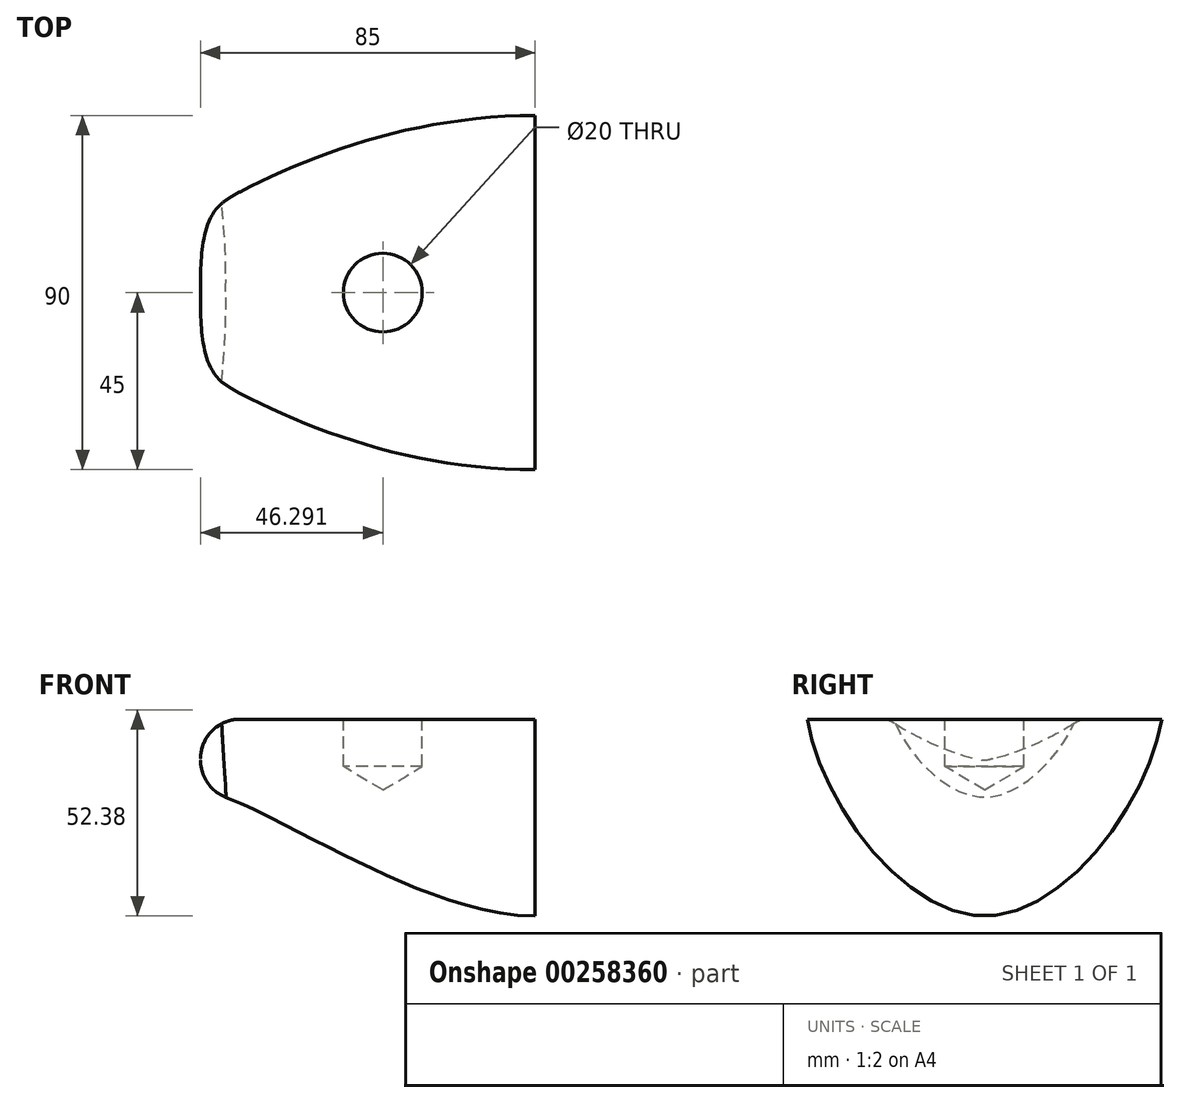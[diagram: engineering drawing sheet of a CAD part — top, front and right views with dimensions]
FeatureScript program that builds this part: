
annotation { "Feature Type Name" : "Feature", "Feature Type Description" : "" }
export const myFeature = defineFeature(function(context is Context, id is Id, definition is map)
    precondition{}
    {
        {
            var Q0;
            Q0=qCreatedBy(makeId("Right.planeOp"),FACE);
            cPlane(context, id + "F0", {"entities" : qUnion([Q0]), "cplaneType" : CPlaneType.OFFSET, "offset" : 85 * mm, "oppositeDirection" : true, "width" : 150 * mm, "height" : 150 * mm});
        }
        {
            var Q0;
            Q0=qCreatedBy(makeId("Right.planeOp"),FACE);
            var sketch = newSketch(context, id + "F1", { "sketchPlane" : qUnion([Q0])});
            skFitSpline(sketch, "E0", {"points": [v(-45, 0) * mm, v(0, -50) * mm, v(45, 0) * mm], "startDerivative": vector(18, -120) * mm, "endDerivative": vector(18, 120) * mm});
            skLineSegment(sketch, "E1", {"start": v(45, 0) * mm, "end": v(-45, 0) * mm});
            skPoint(sketch, "E2", {"position": v(0, 0) * mm});
            skSolve(sketch);
        }
        {
            var Q0;
            Q0=qCreatedBy(id+"F0.planeOp",FACE);
            var sketch = newSketch(context, id + "F2", { "sketchPlane" : qUnion([Q0])});
            skFitSpline(sketch, "E3", {"points": [v(-20, 0) * mm, v(0, -18) * mm, v(20, 0) * mm], "startDerivative": vector(12, -30) * mm, "endDerivative": vector(12, 30) * mm});
            skLineSegment(sketch, "E4", {"start": v(-20, 0) * mm, "end": v(20, 0) * mm});
            skLineSegment(sketch, "E5", {"start": v(20, 0) * mm, "end": v(-20, 0) * mm});
            skPoint(sketch, "E6", {"position": v(0, 0) * mm});
            skPoint(sketch, "E7.0", {"position": v(0, -50) * mm});
            skSolve(sketch);
        }
        {
            var Q0;
            Q0=qCreatedBy(makeId("Top.planeOp"),FACE);
            var sketch = newSketch(context, id + "F3", { "sketchPlane" : qUnion([Q0])});
            skPoint(sketch, "E8", {"position": v(0, -45) * mm});
            skPoint(sketch, "E9", {"position": v(0, 0) * mm});
            skPoint(sketch, "E10", {"position": v(0, 45) * mm});
            skPoint(sketch, "E11.orphan", {"position": v(-102.76, 0) * mm});
            skPoint(sketch, "E12.endDerivative.orphan", {"position": v(-78.5, -38.65) * mm});
            skPoint(sketch, "E13.MirrorCS.end.orphan", {"position": v(-85, 20) * mm});
            skPoint(sketch, "E14.end.orphan", {"position": v(-85, -20) * mm});
            skPoint(sketch, "E15.endDerivative.orphan", {"position": v(-65, 32) * mm});
            skPoint(sketch, "E15.startDerivative.orphan", {"position": v(-35, 45) * mm});
            skFitSpline(sketch, "E16", {"points": [v(-85, -20) * mm, v(0, -45) * mm], "startDerivative": vector(60, -36) * mm, "endDerivative": vector(105, 0) * mm});
            skFitSpline(sketch, "E17.MirrorCS", {"points": [v(-85, 20) * mm, v(0, 45) * mm], "startDerivative": vector(60, 36) * mm, "endDerivative": vector(105, 0) * mm});
            skPoint(sketch, "E18", {"position": v(-37.86, 0) * mm});
            skSolve(sketch);
        }
        {
            var Q0;
            Q0=qCreatedBy(makeId("Front.planeOp"),FACE);
            var sketch = newSketch(context, id + "F4", { "sketchPlane" : qUnion([Q0])});
            skPoint(sketch, "E19.0.internal.orphan", {"position": v(0, -26.5) * mm});
            skPoint(sketch, "E20", {"position": v(-55.09, -17.88) * mm});
            skPoint(sketch, "E21", {"position": v(-55.09, -15.07) * mm});
            skPoint(sketch, "E22.0.internal.orphan", {"position": v(0, -50) * mm});
            skPoint(sketch, "E22.endDerivative.orphan", {"position": v(-70, -20) * mm});
            skPoint(sketch, "E22.startDerivative.orphan", {"position": v(-14.43, -50) * mm});
            skPoint(sketch, "E23.0", {"position": v(-85, -18) * mm});
            skFitSpline(sketch, "E24", {"points": [v(-85, -18) * mm, v(0, -50) * mm], "startDerivative": vector(45, -6) * mm, "endDerivative": vector(89.92, 0) * mm});
            skSolve(sketch);
        }
        {
            var Q0;
            Q0=makeQuery(id+"F1.imprint","IMPRINT",FACE,{"disambiguationData":[TD([[makeQuery(id+"F1.imprint","IMPRINT",EDGE,{"derivedFrom":sQuery(id+"F1.wireOp",EDGE,"E0")}),1.0]])]});
            var Q1;
            Q1=makeQuery(id+"F2.imprint","IMPRINT",FACE,{"disambiguationData":[TD([[makeQuery(id+"F2.imprint","IMPRINT",EDGE,{"derivedFrom":sQuery(id+"F2.wireOp",EDGE,"E3")}),1.0]])]});
            var Q2;
            Q2=sQuery(id+"F3.wireOp",EDGE,"E17.MirrorCS");
            var Q3;
            Q3=sQuery(id+"F3.wireOp",EDGE,"E16");
            var Q4;
            Q4=sQuery(id+"F4.wireOp",EDGE,"E24");
            loft(context, id + "F5", {"addGuides" : true, "sheetProfilesArray" : [{ "sheetProfileEntities" : qUnion([Q0]) }, { "sheetProfileEntities" : qUnion([Q1]) }], "guidesArray" : [{ "guideEntities" : qUnion([Q2]), "guideDerivativeType" : LoftGuideDerivativeType.DEFAULT, "guideDerivativeMagnitude" : 1 }, { "guideEntities" : qUnion([Q3]), "guideDerivativeType" : LoftGuideDerivativeType.DEFAULT, "guideDerivativeMagnitude" : 1 }, { "guideEntities" : qUnion([Q4]), "guideDerivativeType" : LoftGuideDerivativeType.DEFAULT, "guideDerivativeMagnitude" : 1 }]});
        }
        {
            var Q0;
            Q0=makeQuery(id+"F5.opLoft","MID_CAP_EDGE",EDGE,{"disambiguationData":[OSD([sQuery(id+"F2.wireOp",EDGE,"E3"),sQuery(id+"F3.wireOp",EDGE,"E17.MirrorCS"),sQuery(id+"F4.wireOp",EDGE,"E24")])],"capPos":1.0});
            fillet(context, id + "F6", {"entities" : qUnion([Q0]), "radius" : 10 * mm, "tangentPropagation" : true, "allowEdgeOverflow" : false});
        }
        {
            var Q0;
            Q0=qCreatedBy(makeId("Top.planeOp"),FACE);
            var sketch = newSketch(context, id + "F7", { "sketchPlane" : qUnion([Q0])});
            skLineSegment(sketch, "E25.bottom", {"start": v(-61.65, 26.63) * mm, "end": v(6.05, 26.63) * mm});
            skLineSegment(sketch, "E25.top", {"start": v(-61.65, -18.41) * mm, "end": v(6.05, -18.41) * mm});
            skLineSegment(sketch, "E25.left", {"start": v(-61.65, 26.63) * mm, "end": v(-61.65, -18.41) * mm});
            skLineSegment(sketch, "E25.right", {"start": v(6.05, 26.63) * mm, "end": v(6.05, -18.41) * mm});
            skPoint(sketch, "E26", {"position": v(-38.7, 0) * mm});
            skSolve(sketch);
        }
        {
            var Q0;
            Q0=sQuery(id+"F7.wireOp",VERTEX,"E26");
            var Q1;
            Q1=makeQuery(id+"F5.opLoft","SWEPT_BODY",BODY,{"disambiguationData":[OSD([makeQuery(id+"F1.imprint","IMPRINT",FACE,{"disambiguationData":[TD([[makeQuery(id+"F1.imprint","IMPRINT",EDGE,{"derivedFrom":sQuery(id+"F1.wireOp",EDGE,"E0")}),1.0]])]}),makeQuery(id+"F2.imprint","IMPRINT",FACE,{"disambiguationData":[TD([[makeQuery(id+"F2.imprint","IMPRINT",EDGE,{"derivedFrom":sQuery(id+"F2.wireOp",EDGE,"E3")}),1.0]])]}),sQuery(id+"F3.wireOp",EDGE,"E17.MirrorCS"),sQuery(id+"F3.wireOp",EDGE,"E16"),sQuery(id+"F4.wireOp",EDGE,"E24")])]});
            hole(context, id + "F8", {"style" : HoleStyle.C_BORE, "endStyle" : HoleEndStyle.BLIND, "holeDiameter" : 20 * mm, "cBoreDiameter" : 20 * mm, "cBoreDepth" : 5 * mm, "holeDepth" : 12 * mm, "tappedDepth" : 12 * mm, "tapClearance" : 3, "startFromSketch" : true, "locations" : qUnion([Q0]), "scope" : qUnion([Q1])});
        }
    });
